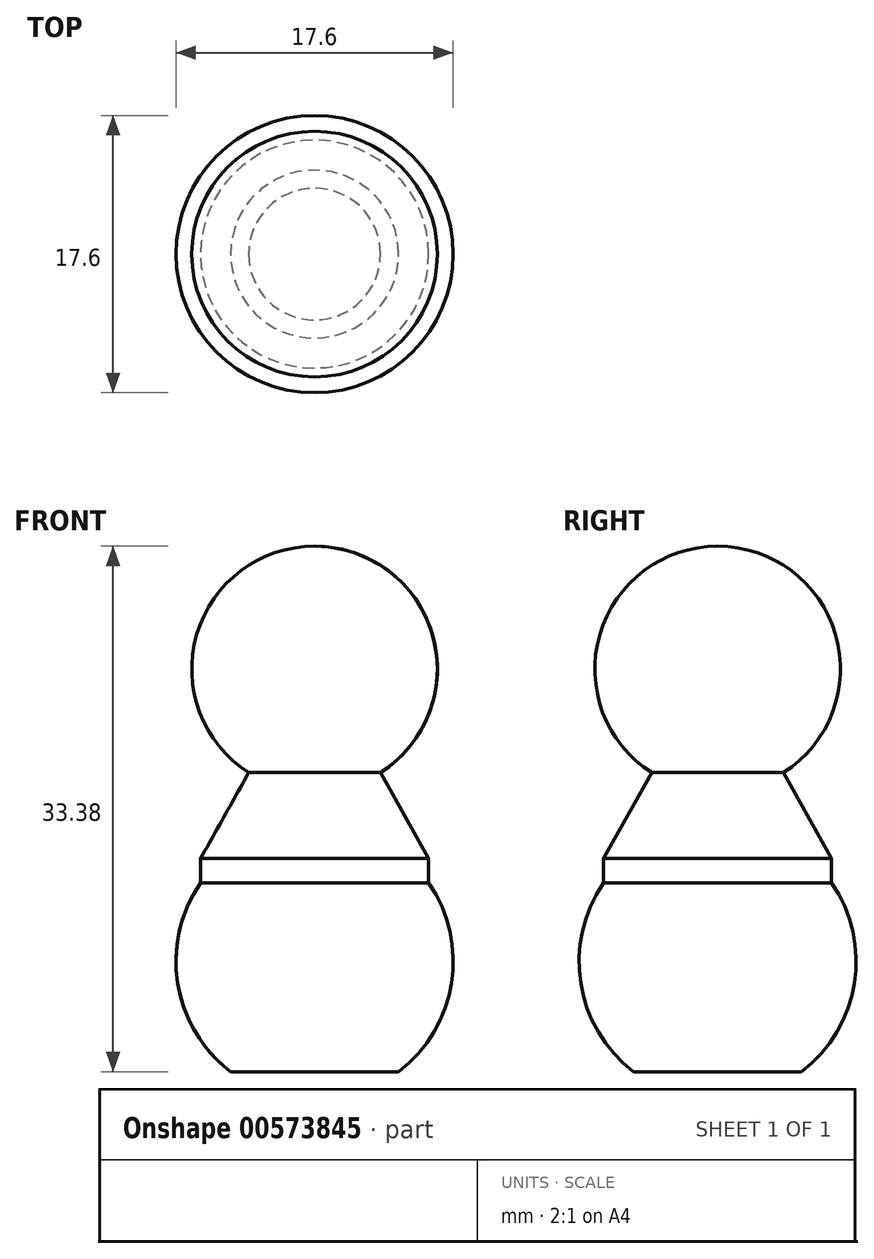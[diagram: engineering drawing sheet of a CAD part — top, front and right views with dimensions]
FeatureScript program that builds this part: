
annotation { "Feature Type Name" : "Feature", "Feature Type Description" : "" }
export const myFeature = defineFeature(function(context is Context, id is Id, definition is map)
    precondition{}
    {
        {
            var Q0;
            Q0=qCreatedBy(makeId("Front.planeOp"),FACE);
            var sketch = newSketch(context, id + "F0", { "sketchPlane" : qUnion([Q0])});
            skLineSegment(sketch, "E0", {"start": v(0, 0) * mm, "end": v(0, 7) * mm});
            skCircle(sketch, "E1", {"center": v(0, 7) * mm, "radius": 8.8 * mm});
            skLineSegment(sketch, "E2", {"start": v(0, 7) * mm, "end": v(0, 15.8) * mm});
            skCircle(sketch, "E3", {"center": v(0, 25.58) * mm, "radius": 7.8 * mm});
            skLineSegment(sketch, "E4", {"start": v(0, 25.58) * mm, "end": v(0, 33.38) * mm});
            skLineSegment(sketch, "E5", {"start": v(0, 25.58) * mm, "end": v(0, 15.8) * mm});
            skLineSegment(sketch, "E6", {"start": v(0, 12) * mm, "end": v(7.24, 12) * mm});
            skLineSegment(sketch, "E7", {"start": v(7.24, 12) * mm, "end": v(7.24, 13.53) * mm});
            skLineSegment(sketch, "E8", {"start": v(7.24, 13.53) * mm, "end": v(4.19, 19) * mm});
            skLineSegment(sketch, "E9", {"start": v(5.33, 0) * mm, "end": v(0, 0) * mm});
            skSolve(sketch);
        }
        {
            var Q0;
            {var subQ2=sQuery(id+"F0.wireOp",EDGE,"E0");Q0=makeQuery(id+"F0.imprint","IMPRINT",FACE,{"disambiguationData":[TD([[makeQuery(id+"F0.imprint","IMPRINT",EDGE,{"derivedFrom":subQ2}),-1.0]])]});}
            var Q1;
            {var subQ3=sQuery(id+"F0.wireOp",EDGE,"E6");Q1=makeQuery(id+"F0.imprint","IMPRINT",FACE,{"disambiguationData":[TD([[makeQuery(id+"F0.imprint","IMPRINT",EDGE,{"derivedFrom":subQ3}),1.0]])]});}
            var Q2;
            {var subQ0=sQuery(id+"F0.wireOp",EDGE,"E7");Q2=makeQuery(id+"F0.imprint","IMPRINT",FACE,{"disambiguationData":[TD([[makeQuery(id+"F0.imprint","IMPRINT",EDGE,{"derivedFrom":subQ0}),1.0]])]});}
            var Q3;
            {var subQ4=sQuery(id+"F0.wireOp",EDGE,"E4");Q3=makeQuery(id+"F0.imprint","IMPRINT",FACE,{"disambiguationData":[TD([[makeQuery(id+"F0.imprint","IMPRINT",EDGE,{"derivedFrom":subQ4}),-1.0]])]});}
            var Q4;
            Q4=sQuery(id+"F0.wireOp",EDGE,"E2");
            revolve(context, id + "F1", {"entities" : qUnion([Q0, Q1, Q2, Q3]), "axis" : qUnion([Q4]), "revolveType" : RevolveType.FULL});
        }
    });
